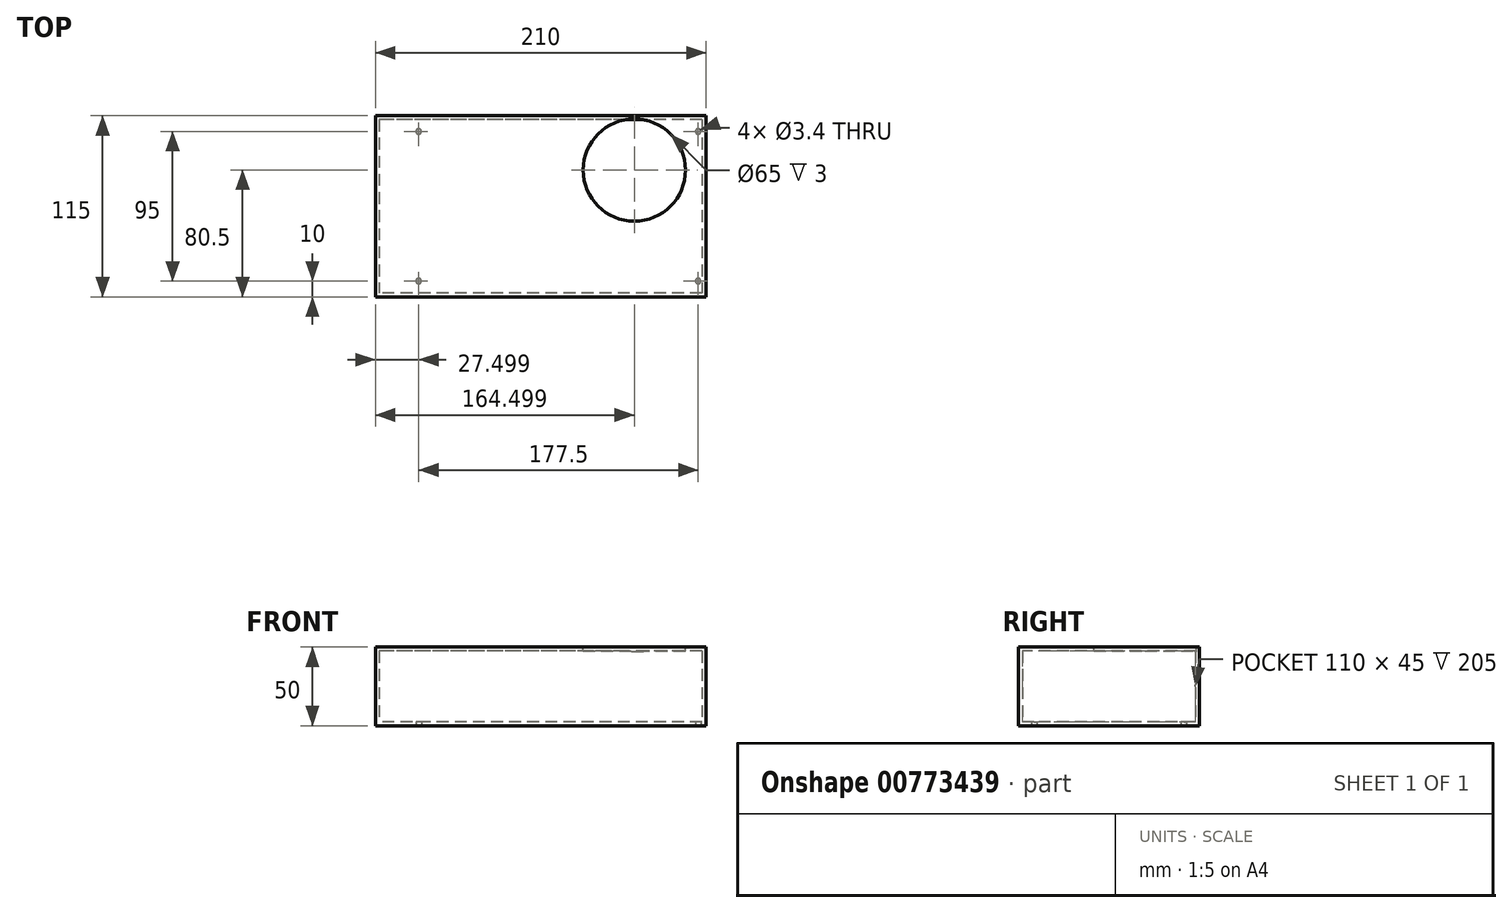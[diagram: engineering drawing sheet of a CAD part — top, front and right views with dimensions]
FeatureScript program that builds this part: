
annotation { "Feature Type Name" : "Feature", "Feature Type Description" : "" }
export const myFeature = defineFeature(function(context is Context, id is Id, definition is map)
    precondition{}
    {
        {
            var Q0;
            Q0=qCreatedBy(makeId("Top.planeOp"),FACE);
            var sketch = newSketch(context, id + "F0", { "sketchPlane" : qUnion([Q0])});
            skLineSegment(sketch, "E0.bottom", {"start": v(94.84, 57.5) * mm, "end": v(-115.16, 57.5) * mm});
            skLineSegment(sketch, "E0.top", {"start": v(94.84, -57.5) * mm, "end": v(-115.16, -57.5) * mm});
            skLineSegment(sketch, "E0.left", {"start": v(94.84, 57.5) * mm, "end": v(94.84, -57.5) * mm});
            skLineSegment(sketch, "E0.right", {"start": v(-115.16, 57.5) * mm, "end": v(-115.16, -57.5) * mm});
            skPoint(sketch, "E0.middle", {"position": v(-10.16, 0) * mm});
            skSolve(sketch);
        }
        {
            var Q0;
            Q0 = qSketchRegion(id + "F0", true);
            extrude(context, id + "F1", {"entities" : qUnion([Q0]), "depth" : 50 * mm, "offsetDistance" : 25 * mm});
        }
        {
            var Q0;
            Q0=makeQuery(id+"F1.opExtrude","CAP_FACE",FACE,{"disambiguationData":[OSD([sQuery(id+"F0.wireOp",EDGE,"E0.bottom"),sQuery(id+"F0.wireOp",EDGE,"E0.top"),sQuery(id+"F0.wireOp",EDGE,"E0.left"),sQuery(id+"F0.wireOp",EDGE,"E0.right")])],"isStart":false});
            var sketch = newSketch(context, id + "F2", { "sketchPlane" : qUnion([Q0])});
            skLineSegment(sketch, "E1.bottom", {"start": v(94.84, 57.5) * mm, "end": v(49.34, 57.5) * mm, "construction": true});
            skLineSegment(sketch, "E1.top", {"start": v(94.84, 23) * mm, "end": v(49.34, 23) * mm, "construction": true});
            skLineSegment(sketch, "E1.left", {"start": v(94.84, 57.5) * mm, "end": v(94.84, 23) * mm, "construction": true});
            skLineSegment(sketch, "E1.right", {"start": v(49.34, 57.5) * mm, "end": v(49.34, 23) * mm, "construction": true});
            skCircle(sketch, "E2", {"center": v(49.34, 23) * mm, "radius": 32.5 * mm});
            skSolve(sketch);
        }
        {
            var Q0;
            Q0=makeQuery(id+"F1.opExtrude","CAP_FACE",FACE,{"disambiguationData":[OSD([sQuery(id+"F0.wireOp",EDGE,"E0.bottom"),sQuery(id+"F0.wireOp",EDGE,"E0.top"),sQuery(id+"F0.wireOp",EDGE,"E0.left"),sQuery(id+"F0.wireOp",EDGE,"E0.right")])],"isStart":false});
            var Q1;
            Q1=makeQuery(id+"F1.opExtrude","SWEPT_BODY",BODY,{"disambiguationData":[OSD([sQuery(id+"F0.wireOp",EDGE,"E0.bottom"),sQuery(id+"F0.wireOp",EDGE,"E0.top"),sQuery(id+"F0.wireOp",EDGE,"E0.left"),sQuery(id+"F0.wireOp",EDGE,"E0.right")])]});
            shell(context, id + "F3", {"isHollow" : true, "entities" : qUnion([Q0]), "parts" : qUnion([Q1]), "thickness" : 2.5 * mm});
        }
        {
            var Q0;
            Q0=makeQuery(id+"F2.imprint","IMPRINT",FACE,{"disambiguationData":[TD([[makeQuery(id+"F2.imprint","IMPRINT",EDGE,{"derivedFrom":sQuery(id+"F2.wireOp",EDGE,"E2")}),1.0]])]});
            extrude(context, id + "F4", {"entities" : qUnion([Q0]), "operationType" : NewBodyOperationType.REMOVE, "oppositeDirection" : true, "depth" : 3 * mm, "offsetDistance" : 25 * mm});
        }
        {
            var Q0;
            Q0=makeQuery(id+"F1.opExtrude","CAP_FACE",FACE,{"disambiguationData":[OSD([sQuery(id+"F0.wireOp",EDGE,"E0.bottom"),sQuery(id+"F0.wireOp",EDGE,"E0.top"),sQuery(id+"F0.wireOp",EDGE,"E0.left"),sQuery(id+"F0.wireOp",EDGE,"E0.right")])],"isStart":true});
            var sketch = newSketch(context, id + "F5", { "sketchPlane" : qUnion([Q0])});
            skLineSegment(sketch, "E3", {"start": v(-115.16, 57.5) * mm, "end": v(-115.16, 47.5) * mm, "construction": true});
            skLineSegment(sketch, "E4", {"start": v(-115.16, 47.5) * mm, "end": v(-87.66, 47.5) * mm, "construction": true});
            skLineSegment(sketch, "E5", {"start": v(-87.66, 47.5) * mm, "end": v(-87.66, -47.5) * mm, "construction": true});
            skLineSegment(sketch, "E6", {"start": v(-87.66, -47.5) * mm, "end": v(89.84, -47.5) * mm, "construction": true});
            skLineSegment(sketch, "E7", {"start": v(-87.66, 47.5) * mm, "end": v(89.84, 47.5) * mm, "construction": true});
            skPoint(sketch, "E8", {"position": v(-87.66, 47.5) * mm});
            skPoint(sketch, "E9", {"position": v(-87.66, -47.5) * mm});
            skPoint(sketch, "E10", {"position": v(89.84, 47.5) * mm});
            skPoint(sketch, "E11", {"position": v(89.84, -47.5) * mm});
            skSolve(sketch);
        }
        {
            var Q0;
            Q0=sQuery(id+"F5.wireOp",VERTEX,"E8");
            var Q1;
            Q1=sQuery(id+"F5.wireOp",VERTEX,"E10");
            var Q2;
            Q2=sQuery(id+"F5.wireOp",VERTEX,"E11");
            var Q3;
            Q3=sQuery(id+"F5.wireOp",VERTEX,"E9");
            var Q4;
            Q4=makeQuery(id+"F1.opExtrude","SWEPT_BODY",BODY,{"disambiguationData":[OSD([sQuery(id+"F0.wireOp",EDGE,"E0.bottom"),sQuery(id+"F0.wireOp",EDGE,"E0.top"),sQuery(id+"F0.wireOp",EDGE,"E0.left"),sQuery(id+"F0.wireOp",EDGE,"E0.right")])]});
            hole(context, id + "F6", {"style" : HoleStyle.SIMPLE, "endStyle" : HoleEndStyle.BLIND, "standardTappedOrClearance" : lookupTablePath({ "fit" : "Normal", "standard" : "ISO", "size" : "M3", "type" : "Clearance" }), "standardBlindInLast" : lookupTablePath({ "fit" : "Normal", "standard" : "ISO", "size" : "M3", "type" : "Clearance" }), "holeDiameter" : 3.4 * mm, "majorDiameter" : 5 * mm, "holeDepth" : 4 * mm, "tappedDepth" : 12 * mm, "tapClearance" : 3, "startFromSketch" : true, "locations" : qUnion([Q0, Q1, Q2, Q3]), "scope" : qUnion([Q4])});
        }
    });
